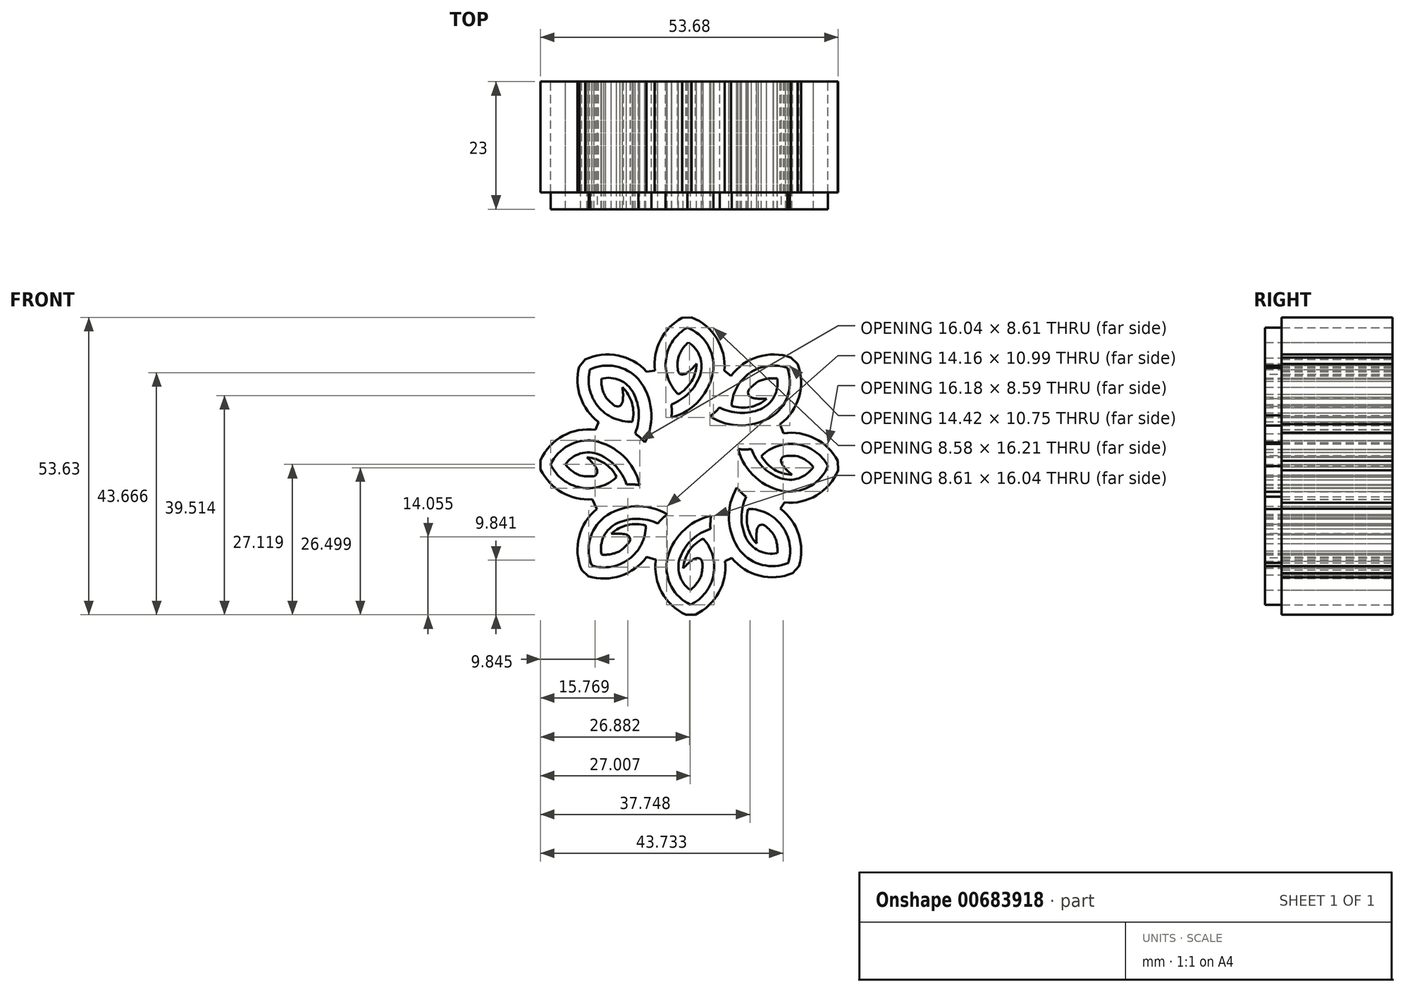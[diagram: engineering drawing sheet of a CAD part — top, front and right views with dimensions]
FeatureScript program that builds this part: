
annotation { "Feature Type Name" : "Feature", "Feature Type Description" : "" }
export const myFeature = defineFeature(function(context is Context, id is Id, definition is map)
    precondition{}
    {
        {
            var Q0;
            Q0=qCreatedBy(makeId("Front.planeOp"),FACE);
            var sketch = newSketch(context, id + "F0", { "sketchPlane" : qUnion([Q0])});
            skArc(sketch, "E0", {"start": v(-80.17, 41.16) * mm, "mid": v(-74.78, 37.03) * mm, "end": v(-68.25, 38.9) * mm});
            skArc(sketch, "E1", {"start": v(-72.35, 45.44) * mm, "mid": v(-76.97, 44.6) * mm, "end": v(-80.17, 41.16) * mm});
            skArc(sketch, "E2", {"start": v(-64.12, 37.47) * mm, "mid": v(-67.04, 42.7) * mm, "end": v(-72.35, 45.44) * mm});
            skArc(sketch, "E3", {"start": v(-64.12, 37.47) * mm, "mid": v(-65.3, 37.58) * mm, "end": v(-66.5, 37.57) * mm});
            skArc(sketch, "E4", {"start": v(-66.5, 37.57) * mm, "mid": v(-68.37, 40.82) * mm, "end": v(-71.45, 42.98) * mm});
            skArc(sketch, "E5", {"start": v(-71.45, 42.98) * mm, "mid": v(-74.8, 43.16) * mm, "end": v(-77.51, 41.2) * mm});
            skArc(sketch, "E6", {"start": v(-77.51, 41.2) * mm, "mid": v(-76.29, 40) * mm, "end": v(-74.78, 39.2) * mm});
            skArc(sketch, "E7", {"start": v(-68.25, 38.9) * mm, "mid": v(-70.45, 41.4) * mm, "end": v(-73.6, 42.48) * mm});
            skFitSpline(sketch, "E8", {"points": [v(-74.78, 39.2) * mm, v(-73.61, 39.05) * mm, v(-72.38, 39.1) * mm, v(-71.86, 39.49) * mm, v(-71.8, 40.18) * mm, v(-72.2, 40.96) * mm, v(-72.77, 41.65) * mm, v(-73.6, 42.48) * mm], "startDerivative": vector(11.1, -2.44) * mm, "endDerivative": vector(-5.58, 5.31) * mm});
            skArc(sketch, "E9", {"start": v(-72.75, 22.97) * mm, "mid": v(-66.05, 24.1) * mm, "end": v(-63, 30.17) * mm});
            skArc(sketch, "E10", {"start": v(-70.58, 31.61) * mm, "mid": v(-73.1, 27.65) * mm, "end": v(-72.75, 22.97) * mm});
            skArc(sketch, "E11", {"start": v(-59.14, 32.23) * mm, "mid": v(-64.95, 33.64) * mm, "end": v(-70.58, 31.61) * mm});
            skArc(sketch, "E12", {"start": v(-59.14, 32.23) * mm, "mid": v(-60.03, 31.44) * mm, "end": v(-60.83, 30.55) * mm});
            skArc(sketch, "E13", {"start": v(-60.83, 30.55) * mm, "mid": v(-64.49, 31.39) * mm, "end": v(-68.16, 30.6) * mm});
            skArc(sketch, "E14", {"start": v(-68.16, 30.6) * mm, "mid": v(-70.56, 28.27) * mm, "end": v(-70.98, 24.94) * mm});
            skArc(sketch, "E15", {"start": v(-70.98, 24.94) * mm, "mid": v(-69.27, 25.03) * mm, "end": v(-67.65, 25.58) * mm});
            skArc(sketch, "E16", {"start": v(-63, 30.17) * mm, "mid": v(-66.32, 30.25) * mm, "end": v(-69.25, 28.68) * mm});
            skFitSpline(sketch, "E17", {"points": [v(-67.65, 25.58) * mm, v(-66.74, 26.34) * mm, v(-65.94, 27.28) * mm, v(-65.88, 27.93) * mm, v(-66.34, 28.44) * mm, v(-67.2, 28.67) * mm, v(-68.08, 28.73) * mm, v(-69.25, 28.68) * mm], "startDerivative": vector(9.33, 6.48) * mm, "endDerivative": vector(-7.69, -0.48) * mm});
            skArc(sketch, "E18", {"start": v(-73.1, 58.3) * mm, "mid": v(-71.62, 51.68) * mm, "end": v(-65.42, 48.92) * mm});
            skArc(sketch, "E19", {"start": v(-64.35, 56.56) * mm, "mid": v(-68.44, 58.89) * mm, "end": v(-73.1, 58.3) * mm});
            skArc(sketch, "E20", {"start": v(-63.18, 45.17) * mm, "mid": v(-62.05, 51.04) * mm, "end": v(-64.35, 56.56) * mm});
            skArc(sketch, "E21", {"start": v(-63.18, 45.17) * mm, "mid": v(-64.01, 46.02) * mm, "end": v(-64.93, 46.77) * mm});
            skArc(sketch, "E22", {"start": v(-64.93, 46.77) * mm, "mid": v(-64.28, 50.47) * mm, "end": v(-65.25, 54.1) * mm});
            skArc(sketch, "E23", {"start": v(-65.25, 54.1) * mm, "mid": v(-67.7, 56.38) * mm, "end": v(-71.03, 56.63) * mm});
            skArc(sketch, "E24", {"start": v(-71.03, 56.63) * mm, "mid": v(-70.87, 54.93) * mm, "end": v(-70.23, 53.34) * mm});
            skArc(sketch, "E25", {"start": v(-65.42, 48.92) * mm, "mid": v(-65.5, 52.24) * mm, "end": v(-67.22, 55.1) * mm});
            skFitSpline(sketch, "E26", {"points": [v(-70.23, 53.34) * mm, v(-69.43, 52.47) * mm, v(-68.46, 51.72) * mm, v(-67.8, 51.69) * mm, v(-67.3, 52.17) * mm, v(-67.13, 53.04) * mm, v(-67.11, 53.92) * mm, v(-67.22, 55.1) * mm], "startDerivative": vector(6.93, -9) * mm, "endDerivative": vector(-0.86, 7.65) * mm});
            skArc(sketch, "E27", {"start": v(-30.17, 40.92) * mm, "mid": v(-35.72, 44.83) * mm, "end": v(-42.16, 42.7) * mm});
            skArc(sketch, "E28", {"start": v(-37.8, 36.32) * mm, "mid": v(-33.22, 37.35) * mm, "end": v(-30.17, 40.92) * mm});
            skArc(sketch, "E29", {"start": v(-46.35, 43.96) * mm, "mid": v(-43.22, 38.85) * mm, "end": v(-37.8, 36.32) * mm});
            skArc(sketch, "E30", {"start": v(-46.35, 43.96) * mm, "mid": v(-45.16, 43.9) * mm, "end": v(-43.97, 43.95) * mm});
            skArc(sketch, "E31", {"start": v(-43.97, 43.95) * mm, "mid": v(-41.96, 40.78) * mm, "end": v(-38.8, 38.75) * mm});
            skArc(sketch, "E32", {"start": v(-38.8, 38.75) * mm, "mid": v(-35.46, 38.7) * mm, "end": v(-32.82, 40.77) * mm});
            skArc(sketch, "E33", {"start": v(-32.82, 40.77) * mm, "mid": v(-34.09, 41.91) * mm, "end": v(-35.63, 42.66) * mm});
            skArc(sketch, "E34", {"start": v(-42.16, 42.7) * mm, "mid": v(-39.86, 40.29) * mm, "end": v(-36.67, 39.34) * mm});
            skFitSpline(sketch, "E35", {"points": [v(-35.63, 42.66) * mm, v(-36.8, 42.76) * mm, v(-38.03, 42.66) * mm, v(-38.54, 42.25) * mm, v(-38.57, 41.56) * mm, v(-38.13, 40.8) * mm, v(-37.54, 40.13) * mm, v(-36.67, 39.34) * mm], "startDerivative": vector(-11.18, 2) * mm, "endDerivative": vector(5.79, -5.08) * mm});
            skArc(sketch, "E36", {"start": v(-37.5, 58.6) * mm, "mid": v(-44.23, 57.7) * mm, "end": v(-47.52, 51.77) * mm});
            skArc(sketch, "E37", {"start": v(-40, 50.04) * mm, "mid": v(-37.32, 53.9) * mm, "end": v(-37.5, 58.6) * mm});
            skArc(sketch, "E38", {"start": v(-51.45, 49.86) * mm, "mid": v(-45.7, 48.23) * mm, "end": v(-40, 50.04) * mm});
            skArc(sketch, "E39", {"start": v(-51.45, 49.86) * mm, "mid": v(-50.53, 50.62) * mm, "end": v(-49.7, 51.47) * mm});
            skArc(sketch, "E40", {"start": v(-49.7, 51.47) * mm, "mid": v(-46.07, 50.5) * mm, "end": v(-42.38, 51.15) * mm});
            skArc(sketch, "E41", {"start": v(-42.38, 51.15) * mm, "mid": v(-39.89, 53.38) * mm, "end": v(-39.35, 56.69) * mm});
            skArc(sketch, "E42", {"start": v(-39.35, 56.69) * mm, "mid": v(-41.06, 56.67) * mm, "end": v(-42.7, 56.18) * mm});
            skArc(sketch, "E43", {"start": v(-47.52, 51.77) * mm, "mid": v(-44.2, 51.56) * mm, "end": v(-41.2, 53.02) * mm});
            skFitSpline(sketch, "E44", {"points": [v(-42.7, 56.18) * mm, v(-43.63, 55.46) * mm, v(-44.46, 54.55) * mm, v(-44.56, 53.9) * mm, v(-44.11, 53.37) * mm, v(-43.27, 53.11) * mm, v(-42.39, 53.02) * mm, v(-41.2, 53.02) * mm], "startDerivative": vector(-9.57, -6.12) * mm, "endDerivative": vector(7.7, 0.19) * mm});
            skArc(sketch, "E45", {"start": v(-55.5, 65.86) * mm, "mid": v(-59.36, 60.27) * mm, "end": v(-57.16, 53.85) * mm});
            skArc(sketch, "E46", {"start": v(-50.83, 58.27) * mm, "mid": v(-51.9, 62.84) * mm, "end": v(-55.5, 65.86) * mm});
            skArc(sketch, "E47", {"start": v(-58.38, 49.65) * mm, "mid": v(-53.3, 52.83) * mm, "end": v(-50.83, 58.27) * mm});
            skArc(sketch, "E48", {"start": v(-58.38, 49.65) * mm, "mid": v(-58.33, 50.84) * mm, "end": v(-58.4, 52.03) * mm});
            skArc(sketch, "E49", {"start": v(-58.4, 52.03) * mm, "mid": v(-55.25, 54.07) * mm, "end": v(-53.25, 57.25) * mm});
            skArc(sketch, "E50", {"start": v(-53.25, 57.25) * mm, "mid": v(-53.24, 60.6) * mm, "end": v(-55.33, 63.21) * mm});
            skArc(sketch, "E51", {"start": v(-55.33, 63.21) * mm, "mid": v(-56.46, 61.93) * mm, "end": v(-57.2, 60.38) * mm});
            skArc(sketch, "E52", {"start": v(-57.16, 53.85) * mm, "mid": v(-54.78, 56.17) * mm, "end": v(-53.86, 59.37) * mm});
            skFitSpline(sketch, "E53", {"points": [v(-57.2, 60.38) * mm, v(-57.28, 59.2) * mm, v(-57.17, 57.98) * mm, v(-56.75, 57.48) * mm, v(-56.06, 57.45) * mm, v(-55.3, 57.9) * mm, v(-54.64, 58.5) * mm, v(-53.86, 59.37) * mm], "startDerivative": vector(-1.88, -11.2) * mm, "endDerivative": vector(5.02, 5.84) * mm});
            skArc(sketch, "E54", {"start": v(-54.93, 15.9) * mm, "mid": v(-50.8, 21.3) * mm, "end": v(-52.67, 27.82) * mm});
            skArc(sketch, "E55", {"start": v(-59.22, 23.72) * mm, "mid": v(-58.37, 19.1) * mm, "end": v(-54.93, 15.9) * mm});
            skArc(sketch, "E56", {"start": v(-51.24, 31.95) * mm, "mid": v(-56.47, 29.04) * mm, "end": v(-59.22, 23.72) * mm});
            skArc(sketch, "E57", {"start": v(-51.24, 31.95) * mm, "mid": v(-51.36, 30.77) * mm, "end": v(-51.35, 29.58) * mm});
            skArc(sketch, "E58", {"start": v(-51.35, 29.58) * mm, "mid": v(-54.6, 27.7) * mm, "end": v(-56.75, 24.63) * mm});
            skArc(sketch, "E59", {"start": v(-56.75, 24.63) * mm, "mid": v(-56.93, 21.28) * mm, "end": v(-54.98, 18.56) * mm});
            skArc(sketch, "E60", {"start": v(-54.98, 18.56) * mm, "mid": v(-53.78, 19.79) * mm, "end": v(-52.97, 21.3) * mm});
            skArc(sketch, "E61", {"start": v(-52.67, 27.82) * mm, "mid": v(-55.17, 25.62) * mm, "end": v(-56.25, 22.47) * mm});
            skFitSpline(sketch, "E62", {"points": [v(-52.97, 21.3) * mm, v(-52.82, 22.47) * mm, v(-52.87, 23.7) * mm, v(-53.26, 24.22) * mm, v(-53.96, 24.28) * mm, v(-54.73, 23.87) * mm, v(-55.42, 23.31) * mm, v(-56.25, 22.47) * mm], "startDerivative": vector(2.44, 11.1) * mm, "endDerivative": vector(-5.31, -5.58) * mm});
            skArc(sketch, "E63", {"start": v(-37.32, 23.44) * mm, "mid": v(-38.48, 30.13) * mm, "end": v(-44.54, 33.18) * mm});
            skArc(sketch, "E64", {"start": v(-45.97, 25.6) * mm, "mid": v(-42, 23.08) * mm, "end": v(-37.32, 23.44) * mm});
            skArc(sketch, "E65", {"start": v(-46.6, 37.03) * mm, "mid": v(-48, 31.22) * mm, "end": v(-45.97, 25.6) * mm});
            skArc(sketch, "E66", {"start": v(-46.6, 37.03) * mm, "mid": v(-45.81, 36.15) * mm, "end": v(-44.93, 35.35) * mm});
            skArc(sketch, "E67", {"start": v(-44.93, 35.35) * mm, "mid": v(-45.76, 31.69) * mm, "end": v(-44.96, 28.02) * mm});
            skArc(sketch, "E68", {"start": v(-44.96, 28.02) * mm, "mid": v(-42.62, 25.62) * mm, "end": v(-39.3, 25.21) * mm});
            skArc(sketch, "E69", {"start": v(-39.3, 25.21) * mm, "mid": v(-39.39, 26.92) * mm, "end": v(-39.95, 28.54) * mm});
            skArc(sketch, "E70", {"start": v(-44.54, 33.18) * mm, "mid": v(-44.62, 29.86) * mm, "end": v(-43.04, 26.93) * mm});
            skFitSpline(sketch, "E71", {"points": [v(-39.95, 28.54) * mm, v(-40.7, 29.44) * mm, v(-41.64, 30.24) * mm, v(-42.3, 30.3) * mm, v(-42.8, 29.84) * mm, v(-43.03, 28.99) * mm, v(-43.09, 28.1) * mm, v(-43.04, 26.93) * mm], "startDerivative": vector(-6.5, 9.32) * mm, "endDerivative": vector(0.5, -7.69) * mm});
            skArc(sketch, "E72.0", {"start": v(-56.46, 67.62) * mm, "mid": v(-60.37, 63.62) * mm, "end": v(-61.37, 58.13) * mm});
            skArc(sketch, "E73.0", {"start": v(-48.84, 58.1) * mm, "mid": v(-50.2, 63.9) * mm, "end": v(-54.77, 67.72) * mm});
            skArc(sketch, "E74.0", {"start": v(-62.87, 57.9) * mm, "mid": v(-68.05, 60.85) * mm, "end": v(-73.96, 60.11) * mm});
            skArc(sketch, "E75.0", {"start": v(-75.03, 58.8) * mm, "mid": v(-74.79, 53.28) * mm, "end": v(-71.52, 48.83) * mm});
            skArc(sketch, "E76.0", {"start": v(-72.07, 47.42) * mm, "mid": v(-77.93, 46.35) * mm, "end": v(-81.99, 41.99) * mm});
            skArc(sketch, "E77.0", {"start": v(-81.97, 40.29) * mm, "mid": v(-78.14, 36.17) * mm, "end": v(-72.65, 34.92) * mm});
            skArc(sketch, "E78.0", {"start": v(-71.84, 33.16) * mm, "mid": v(-75.04, 28.13) * mm, "end": v(-74.6, 22.2) * mm});
            skArc(sketch, "E79.0", {"start": v(-73.33, 21.05) * mm, "mid": v(-67.55, 21.11) * mm, "end": v(-62.87, 24.5) * mm});
            skArc(sketch, "E80.0", {"start": v(-61.2, 24) * mm, "mid": v(-60.13, 18.14) * mm, "end": v(-55.76, 14.09) * mm});
            skArc(sketch, "E81.0", {"start": v(-54.06, 14.1) * mm, "mid": v(-49.87, 18.07) * mm, "end": v(-48.72, 23.74) * mm});
            skArc(sketch, "E82.0", {"start": v(-47.52, 24.33) * mm, "mid": v(-42.48, 21.14) * mm, "end": v(-36.54, 21.6) * mm});
            skArc(sketch, "E83.0", {"start": v(-35.4, 22.86) * mm, "mid": v(-35.45, 28.57) * mm, "end": v(-38.74, 33.23) * mm});
            skArc(sketch, "E84.0", {"start": v(-38, 34.33) * mm, "mid": v(-32.19, 35.64) * mm, "end": v(-28.31, 40.16) * mm});
            skArc(sketch, "E85.0", {"start": v(-28.4, 41.86) * mm, "mid": v(-32.51, 45.88) * mm, "end": v(-38.19, 46.81) * mm});
            skArc(sketch, "E86.0", {"start": v(-38.8, 48.44) * mm, "mid": v(-35.4, 53.35) * mm, "end": v(-35.63, 59.3) * mm});
            skArc(sketch, "E87.0", {"start": v(-36.84, 60.49) * mm, "mid": v(-42.8, 60.6) * mm, "end": v(-47.66, 57.15) * mm});
            skLineSegment(sketch, "E88", {"start": v(-38.8, 48.44) * mm, "end": v(-38.19, 46.81) * mm});
            skLineSegment(sketch, "E89", {"start": v(-38, 34.33) * mm, "end": v(-38.74, 33.23) * mm});
            skLineSegment(sketch, "E90", {"start": v(-28.4, 41.86) * mm, "end": v(-28.31, 40.16) * mm});
            skLineSegment(sketch, "E91", {"start": v(-48.84, 58.1) * mm, "end": v(-47.66, 57.15) * mm});
            skLineSegment(sketch, "E92", {"start": v(-62.87, 57.9) * mm, "end": v(-61.37, 58.13) * mm});
            skLineSegment(sketch, "E93", {"start": v(-56.46, 67.62) * mm, "end": v(-54.77, 67.72) * mm});
            skLineSegment(sketch, "E94", {"start": v(-36.84, 60.49) * mm, "end": v(-35.63, 59.3) * mm});
            skLineSegment(sketch, "E95", {"start": v(-75.03, 58.8) * mm, "end": v(-73.96, 60.11) * mm});
            skLineSegment(sketch, "E96", {"start": v(-72.07, 47.42) * mm, "end": v(-71.52, 48.83) * mm});
            skLineSegment(sketch, "E97", {"start": v(-81.97, 40.29) * mm, "end": v(-81.99, 41.99) * mm});
            skLineSegment(sketch, "E98", {"start": v(-71.84, 33.16) * mm, "end": v(-72.65, 34.92) * mm});
            skLineSegment(sketch, "E99", {"start": v(-74.6, 22.2) * mm, "end": v(-73.33, 21.05) * mm});
            skLineSegment(sketch, "E100", {"start": v(-61.2, 24) * mm, "end": v(-62.87, 24.5) * mm});
            skLineSegment(sketch, "E101", {"start": v(-55.76, 14.09) * mm, "end": v(-54.06, 14.1) * mm});
            skLineSegment(sketch, "E102", {"start": v(-47.52, 24.33) * mm, "end": v(-48.72, 23.74) * mm});
            skLineSegment(sketch, "E103", {"start": v(-35.4, 22.86) * mm, "end": v(-36.54, 21.6) * mm});
            skSolve(sketch);
        }
        {
            var Q0;
            Q0=makeQuery(id+"F0.imprint","IMPRINT",FACE,{"disambiguationData":[TD([[makeQuery(id+"F0.imprint","IMPRINT",EDGE,{"derivedFrom":sQuery(id+"F0.wireOp",EDGE,"E18")}),1.0]])]});
            var Q1;
            Q1=makeQuery(id+"F0.imprint","IMPRINT",FACE,{"disambiguationData":[TD([[makeQuery(id+"F0.imprint","IMPRINT",EDGE,{"derivedFrom":sQuery(id+"F0.wireOp",EDGE,"E0")}),1.0]])]});
            var Q2;
            Q2=makeQuery(id+"F0.imprint","IMPRINT",FACE,{"disambiguationData":[TD([[makeQuery(id+"F0.imprint","IMPRINT",EDGE,{"derivedFrom":sQuery(id+"F0.wireOp",EDGE,"E9")}),1.0]])]});
            var Q3;
            Q3=makeQuery(id+"F0.imprint","IMPRINT",FACE,{"disambiguationData":[TD([[makeQuery(id+"F0.imprint","IMPRINT",EDGE,{"derivedFrom":sQuery(id+"F0.wireOp",EDGE,"E54")}),1.0]])]});
            var Q4;
            Q4=makeQuery(id+"F0.imprint","IMPRINT",FACE,{"disambiguationData":[TD([[makeQuery(id+"F0.imprint","IMPRINT",EDGE,{"derivedFrom":sQuery(id+"F0.wireOp",EDGE,"E63")}),1.0]])]});
            var Q5;
            Q5=makeQuery(id+"F0.imprint","IMPRINT",FACE,{"disambiguationData":[TD([[makeQuery(id+"F0.imprint","IMPRINT",EDGE,{"derivedFrom":sQuery(id+"F0.wireOp",EDGE,"E27")}),1.0]])]});
            var Q6;
            Q6=makeQuery(id+"F0.imprint","IMPRINT",FACE,{"disambiguationData":[TD([[makeQuery(id+"F0.imprint","IMPRINT",EDGE,{"derivedFrom":sQuery(id+"F0.wireOp",EDGE,"E36")}),1.0]])]});
            var Q7;
            Q7=makeQuery(id+"F0.imprint","IMPRINT",FACE,{"disambiguationData":[TD([[makeQuery(id+"F0.imprint","IMPRINT",EDGE,{"derivedFrom":sQuery(id+"F0.wireOp",EDGE,"E45")}),1.0]])]});
            extrude(context, id + "F1", {"entities" : qUnion([Q0, Q1, Q2, Q3, Q4, Q5, Q6, Q7]), "depth" : 23 * mm, "offsetDistance" : 25 * mm});
        }
        {
            var Q0;
            Q0=makeQuery(id+"F0.imprint","IMPRINT",FACE,{"disambiguationData":[TD([[makeQuery(id+"F0.imprint","IMPRINT",EDGE,{"derivedFrom":sQuery(id+"F0.wireOp",EDGE,"E0")}),-1.0]])]});
            extrude(context, id + "F2", {"entities" : qUnion([Q0]), "depth" : 20 * mm, "offsetDistance" : 25 * mm});
        }
    });
